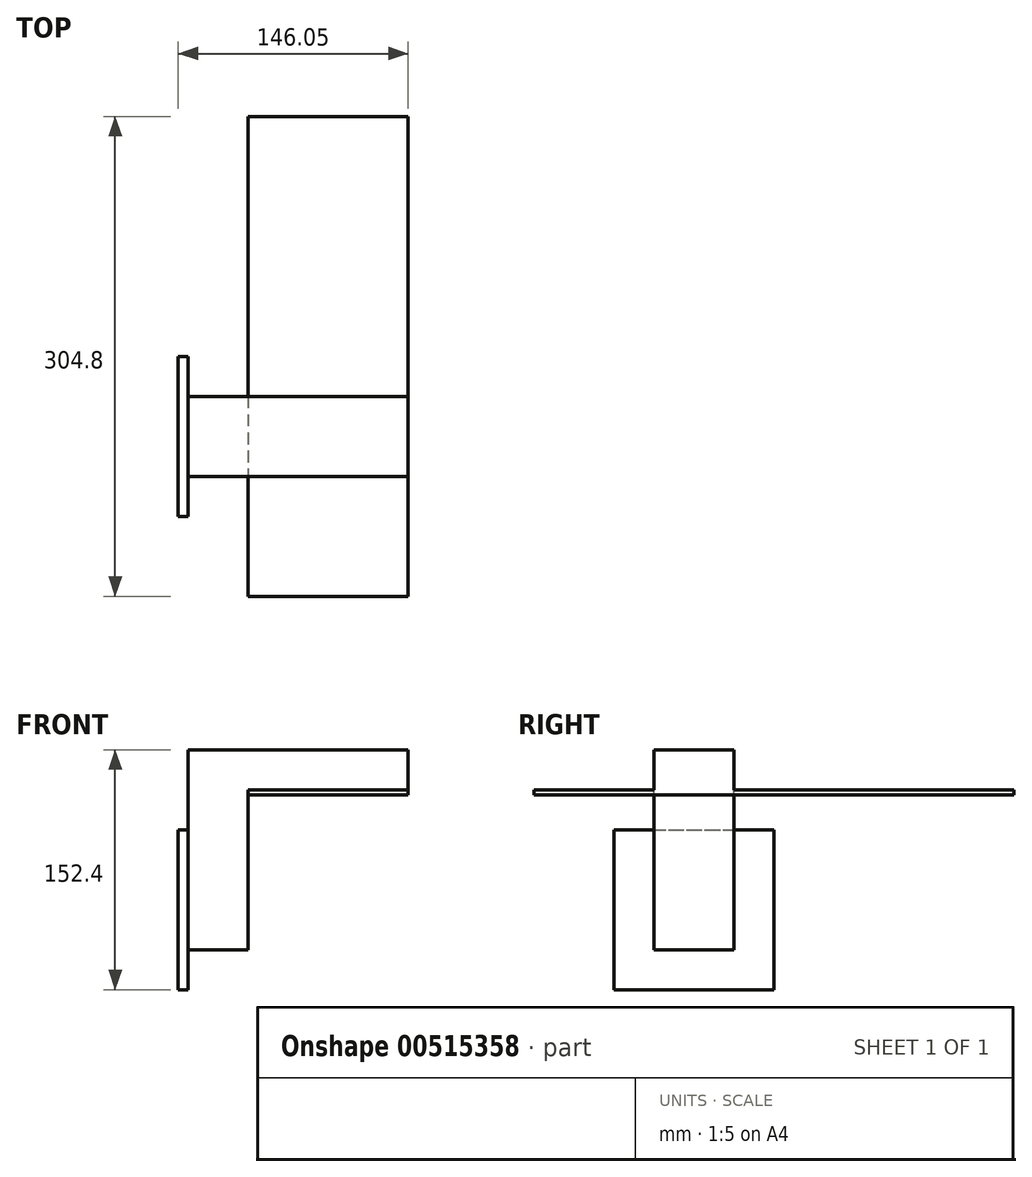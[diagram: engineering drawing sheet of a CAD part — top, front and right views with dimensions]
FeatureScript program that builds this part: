
annotation { "Feature Type Name" : "Feature", "Feature Type Description" : "" }
export const myFeature = defineFeature(function(context is Context, id is Id, definition is map)
    precondition{}
    {
        {
            var Q0;
            Q0=qCreatedBy(makeId("Top.planeOp"),FACE);
            var sketch = newSketch(context, id + "F0", { "sketchPlane" : qUnion([Q0])});
            skLineSegment(sketch, "E0.bottom", {"start": v(-33.13, 161.2) * mm, "end": v(68.47, 161.2) * mm});
            skLineSegment(sketch, "E0.top", {"start": v(-33.13, -143.6) * mm, "end": v(68.47, -143.6) * mm});
            skLineSegment(sketch, "E0.left", {"start": v(-33.13, 161.2) * mm, "end": v(-33.13, -143.6) * mm});
            skLineSegment(sketch, "E0.right", {"start": v(68.47, 161.2) * mm, "end": v(68.47, -143.6) * mm});
            skSolve(sketch);
        }
        {
            var Q0;
            Q0 = qSketchRegion(id + "F0", true);
            extrude(context, id + "F1", {"entities" : qUnion([Q0]), "depth" : 3.17 * mm, "offsetDistance" : 25.4 * mm});
        }
        {
            var Q0;
            Q0=makeQuery(id+"F1.opExtrude","CAP_FACE",FACE,{"disambiguationData":[OSD([sQuery(id+"F0.wireOp",EDGE,"E0.bottom"),sQuery(id+"F0.wireOp",EDGE,"E0.top"),sQuery(id+"F0.wireOp",EDGE,"E0.left"),sQuery(id+"F0.wireOp",EDGE,"E0.right")])],"isStart":false});
            var sketch = newSketch(context, id + "F2", { "sketchPlane" : qUnion([Q0])});
            skLineSegment(sketch, "E1", {"start": v(-33.13, -143.6) * mm, "end": v(-33.13, 8.8) * mm});
            skLineSegment(sketch, "E2.bottom", {"start": v(-33.13, -67.4) * mm, "end": v(68.47, -67.4) * mm});
            skLineSegment(sketch, "E2.top", {"start": v(-33.13, -16.6) * mm, "end": v(68.47, -16.6) * mm});
            skLineSegment(sketch, "E2.left", {"start": v(-33.13, -67.4) * mm, "end": v(-33.13, -16.6) * mm});
            skLineSegment(sketch, "E2.right", {"start": v(68.47, -67.4) * mm, "end": v(68.47, -16.6) * mm});
            skLineSegment(sketch, "E3.bottom", {"start": v(-33.13, -16.6) * mm, "end": v(-71.23, -16.6) * mm});
            skLineSegment(sketch, "E3.top", {"start": v(-33.13, -67.4) * mm, "end": v(-71.23, -67.4) * mm});
            skLineSegment(sketch, "E3.left", {"start": v(-33.13, -16.6) * mm, "end": v(-33.13, -67.4) * mm});
            skLineSegment(sketch, "E3.right", {"start": v(-71.23, -16.6) * mm, "end": v(-71.23, -67.4) * mm});
            skSolve(sketch);
        }
        {
            var Q0;
            Q0=makeQuery(id+"F2.imprint","IMPRINT",FACE,{"disambiguationData":[TD([[makeQuery(id+"F2.imprint","IMPRINT",EDGE,{"derivedFrom":sQuery(id+"F2.wireOp",EDGE,"E3.bottom")}),1.0]])]});
            var Q1;
            Q1=makeQuery(id+"F2.imprint","IMPRINT",FACE,{"disambiguationData":[TD([[makeQuery(id+"F2.imprint","IMPRINT",EDGE,{"derivedFrom":sQuery(id+"F2.wireOp",EDGE,"E2.bottom")}),1.0]])]});
            extrude(context, id + "F3", {"entities" : qUnion([Q0, Q1]), "operationType" : NewBodyOperationType.ADD, "depth" : 25.4 * mm, "offsetDistance" : 25.4 * mm});
        }
        {
            var Q0;
            Q0=makeQuery(id+"F3.opExtrude","CAP_FACE",FACE,{"disambiguationData":[OSD([sQuery(id+"F2.wireOp",EDGE,"E2.bottom"),sQuery(id+"F2.wireOp",EDGE,"E2.top"),sQuery(id+"F2.wireOp",EDGE,"E2.right"),sQuery(id+"F2.wireOp",EDGE,"E3.bottom"),sQuery(id+"F2.wireOp",EDGE,"E3.top"),sQuery(id+"F2.wireOp",EDGE,"E3.right")])],"isStart":true});
            extrude(context, id + "F4", {"entities" : qUnion([Q0]), "operationType" : NewBodyOperationType.ADD, "depth" : 101.6 * mm, "offsetDistance" : 25.4 * mm});
        }
        {
            var Q0;
            {var subQ0=sQuery(id+"F2.wireOp",EDGE,"E3.right");Q0=makeQuery(id+"F4.boolean.opBoolean","MERGE",FACE,{"derivedFrom":[makeQuery(id+"F3.opExtrude","SWEPT_FACE",FACE,{"disambiguationData":[OSD([subQ0])]}),makeQuery(id+"F4.opExtrude","SWEPT_FACE",FACE,{"disambiguationData":[OSD([subQ0])]})]});}
            var sketch = newSketch(context, id + "F5", { "sketchPlane" : qUnion([Q0])});
            skLineSegment(sketch, "E4", {"start": v(42, -98.43) * mm, "end": v(42, -73.03) * mm});
            skLineSegment(sketch, "E5.bottom", {"start": v(92.8, -22.23) * mm, "end": v(-8.8, -22.23) * mm});
            skLineSegment(sketch, "E5.top", {"start": v(92.8, -123.83) * mm, "end": v(-8.8, -123.83) * mm});
            skLineSegment(sketch, "E5.left", {"start": v(92.8, -22.23) * mm, "end": v(92.8, -123.83) * mm});
            skLineSegment(sketch, "E5.right", {"start": v(-8.8, -22.23) * mm, "end": v(-8.8, -123.83) * mm});
            skPoint(sketch, "E5.middle", {"position": v(42, -73.03) * mm});
            skSolve(sketch);
        }
        {
            var Q0;
            Q0=makeQuery(id+"F5.imprint","IMPRINT",FACE,{"disambiguationData":[TD([[makeQuery(id+"F5.imprint","IMPRINT",EDGE,{"derivedFrom":sQuery(id+"F5.wireOp",EDGE,"E5.top")}),-1.0]])]});
            var Q1;
            {var subQ0=sQuery(id+"F2.wireOp",EDGE,"E3.right");var subQ3=makeQuery(id+"F4.opExtrude","CAP_EDGE",EDGE,{"disambiguationData":[OSD([subQ0])],"isStart":false});var subQ10=makeQuery(id+"F5.imprint","IMPRINT",VERTEX,{"derivedFrom":subQ3});Q1=makeQuery(id+"F5.imprint","IMPRINT",FACE,{"disambiguationData":[TD([[makeQuery(id+"F5.imprint","IMPRINT",EDGE,{"disambiguationData":[TD([[subQ10,1.0]])],"derivedFrom":subQ3}),1.0]])]});}
            extrude(context, id + "F6", {"entities" : qUnion([Q0, Q1]), "operationType" : NewBodyOperationType.ADD, "depth" : 6.35 * mm, "offsetDistance" : 25.4 * mm});
        }
        {
            var Q0;
            Q0=makeQuery(id+"F6.opExtrude","CAP_FACE",FACE,{"disambiguationData":[OSD([sQuery(id+"F5.wireOp",EDGE,"E5.bottom"),sQuery(id+"F5.wireOp",EDGE,"E5.top"),sQuery(id+"F5.wireOp",EDGE,"E5.left"),sQuery(id+"F5.wireOp",EDGE,"E5.right")])],"isStart":false});
            var sketch = newSketch(context, id + "F7", { "sketchPlane" : qUnion([Q0])});
            skCircle(sketch, "E6", {"center": v(42, -73.03) * mm, "radius": 25.4 * mm});
            skPoint(sketch, "E6.centerSnap0", {"position": v(-8.8, -73.03) * mm});
            skPoint(sketch, "E6.centerSnap1", {"position": v(42, -123.83) * mm});
            skSolve(sketch);
        }
        {
            var Q0;
            Q0=sQuery(id+"F7.wireOp",EDGE,"E6");
            extrude(context, id + "F8", {"bodyType" : ToolBodyType.SURFACE, "surfaceEntities" : qUnion([Q0]), "depth" : 101.6 * mm, "offsetDistance" : 25.4 * mm});
        }
    });
